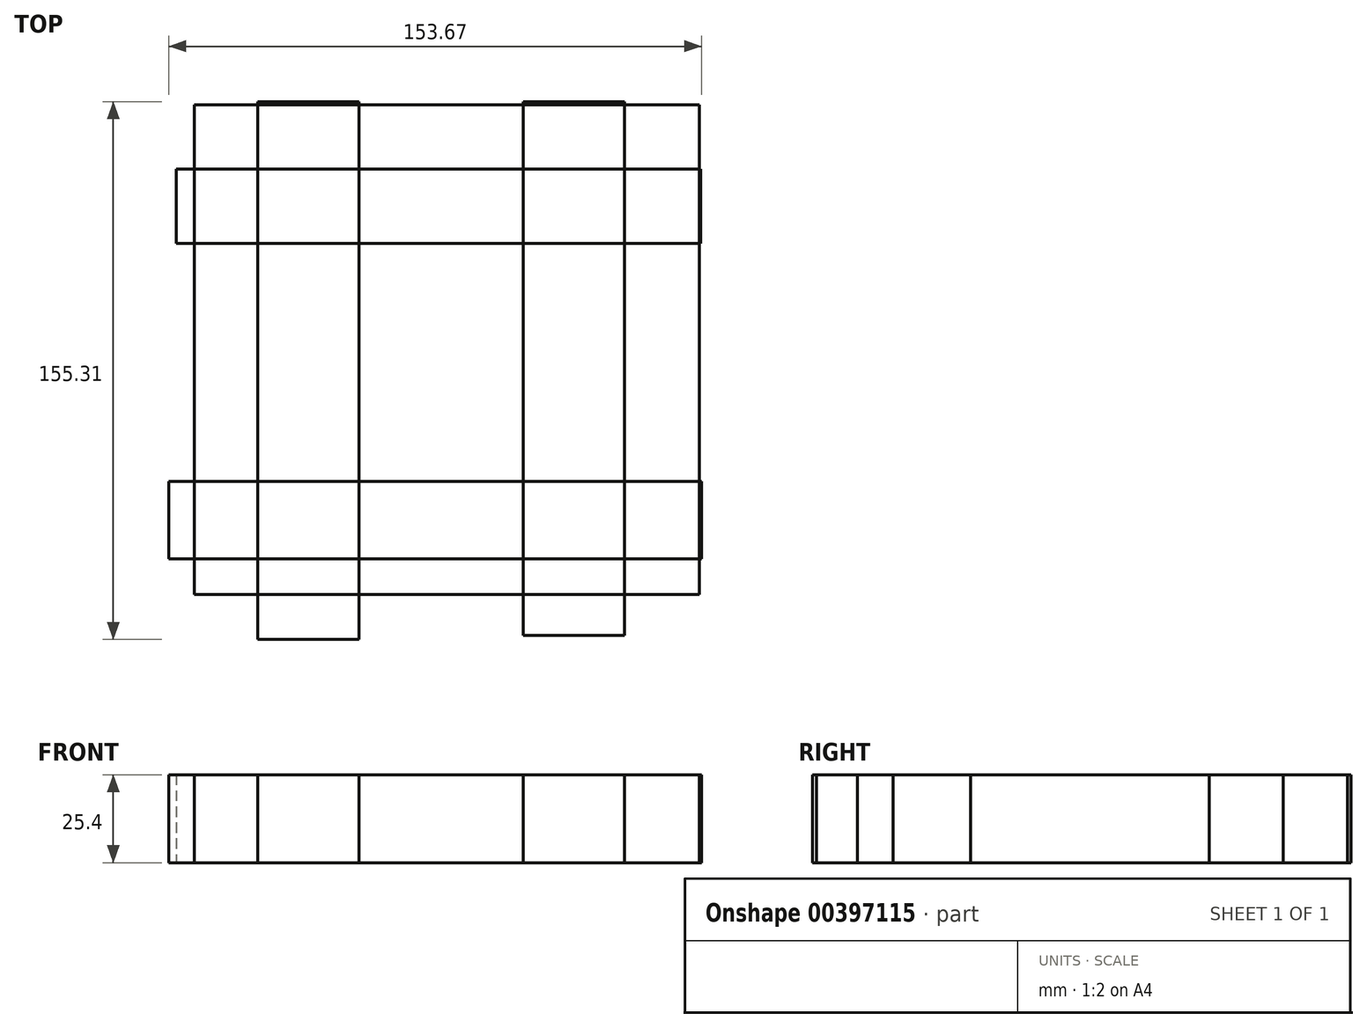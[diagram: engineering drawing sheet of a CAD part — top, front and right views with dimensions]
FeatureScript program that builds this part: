
annotation { "Feature Type Name" : "Feature", "Feature Type Description" : "" }
export const myFeature = defineFeature(function(context is Context, id is Id, definition is map)
    precondition{}
    {
        {
            var Q0;
            Q0=qCreatedBy(makeId("Top.planeOp"),FACE);
            var sketch = newSketch(context, id + "F0", { "sketchPlane" : qUnion([Q0])});
            skLineSegment(sketch, "E0.bottom", {"start": v(-69.67, -66.32) * mm, "end": v(76.01, -66.32) * mm});
            skLineSegment(sketch, "E0.top", {"start": v(-69.67, 75.03) * mm, "end": v(76.01, 75.03) * mm});
            skLineSegment(sketch, "E0.left", {"start": v(-69.67, -66.32) * mm, "end": v(-69.67, 75.03) * mm});
            skLineSegment(sketch, "E0.right", {"start": v(76.01, -66.32) * mm, "end": v(76.01, 75.03) * mm});
            skSolve(sketch);
        }
        {
            var Q0;
            Q0=qCreatedBy(makeId("Top.planeOp"),FACE);
            var sketch = newSketch(context, id + "F1", { "sketchPlane" : qUnion([Q0])});
            skLineSegment(sketch, "E1.bottom", {"start": v(-74.95, 56.48) * mm, "end": v(76.36, 56.48) * mm});
            skLineSegment(sketch, "E1.top", {"start": v(-74.95, 35.06) * mm, "end": v(76.36, 35.06) * mm});
            skLineSegment(sketch, "E1.left", {"start": v(-74.95, 56.48) * mm, "end": v(-74.95, 35.06) * mm});
            skLineSegment(sketch, "E1.right", {"start": v(76.36, 56.48) * mm, "end": v(76.36, 35.06) * mm});
            skSolve(sketch);
        }
        {
            var Q0;
            Q0 = qSketchRegion(id + "F1", true);
            extrude(context, id + "F2", {"entities" : qUnion([Q0]), "depth" : 25.4 * mm});
        }
        {
            var Q0;
            Q0=qCreatedBy(makeId("Top.planeOp"),FACE);
            var sketch = newSketch(context, id + "F3", { "sketchPlane" : qUnion([Q0])});
            skLineSegment(sketch, "E2.bottom", {"start": v(-77.07, -56) * mm, "end": v(76.6, -56) * mm});
            skLineSegment(sketch, "E2.top", {"start": v(-77.07, -33.65) * mm, "end": v(76.6, -33.65) * mm});
            skLineSegment(sketch, "E2.left", {"start": v(-77.07, -56) * mm, "end": v(-77.07, -33.65) * mm});
            skLineSegment(sketch, "E2.right", {"start": v(76.6, -56) * mm, "end": v(76.6, -33.65) * mm});
            skSolve(sketch);
        }
        {
            var Q0;
            Q0 = qSketchRegion(id + "F3", true);
            extrude(context, id + "F4", {"entities" : qUnion([Q0]), "depth" : 25.4 * mm});
        }
        {
            var Q0;
            Q0=qCreatedBy(makeId("Top.planeOp"),FACE);
            var sketch = newSketch(context, id + "F5", { "sketchPlane" : qUnion([Q0])});
            skLineSegment(sketch, "E3.bottom", {"start": v(-51.42, 76) * mm, "end": v(-22.24, 76) * mm});
            skLineSegment(sketch, "E3.top", {"start": v(-51.42, -79.3) * mm, "end": v(-22.24, -79.3) * mm});
            skLineSegment(sketch, "E3.left", {"start": v(-51.42, 76) * mm, "end": v(-51.42, -79.3) * mm});
            skLineSegment(sketch, "E3.right", {"start": v(-22.24, 76) * mm, "end": v(-22.24, -79.3) * mm});
            skSolve(sketch);
        }
        {
            var Q0;
            Q0 = qSketchRegion(id + "F5", true);
            extrude(context, id + "F6", {"entities" : qUnion([Q0]), "depth" : 25.4 * mm});
        }
        {
            var Q0;
            Q0=qCreatedBy(makeId("Top.planeOp"),FACE);
            var sketch = newSketch(context, id + "F7", { "sketchPlane" : qUnion([Q0])});
            skLineSegment(sketch, "E4.bottom", {"start": v(25.1, 76) * mm, "end": v(54.4, 76) * mm});
            skLineSegment(sketch, "E4.top", {"start": v(25.1, -78.15) * mm, "end": v(54.4, -78.15) * mm});
            skLineSegment(sketch, "E4.left", {"start": v(25.1, 76) * mm, "end": v(25.1, -78.15) * mm});
            skLineSegment(sketch, "E4.right", {"start": v(54.4, 76) * mm, "end": v(54.4, -78.15) * mm});
            skSolve(sketch);
        }
        {
            var Q0;
            Q0 = qSketchRegion(id + "F7", true);
            extrude(context, id + "F8", {"entities" : qUnion([Q0]), "depth" : 25.4 * mm});
        }
        {
            var Q0;
            Q0 = qSketchRegion(id + "F0", true);
            extrude(context, id + "F9", {"entities" : qUnion([Q0]), "depth" : 25.4 * mm});
        }
    });
